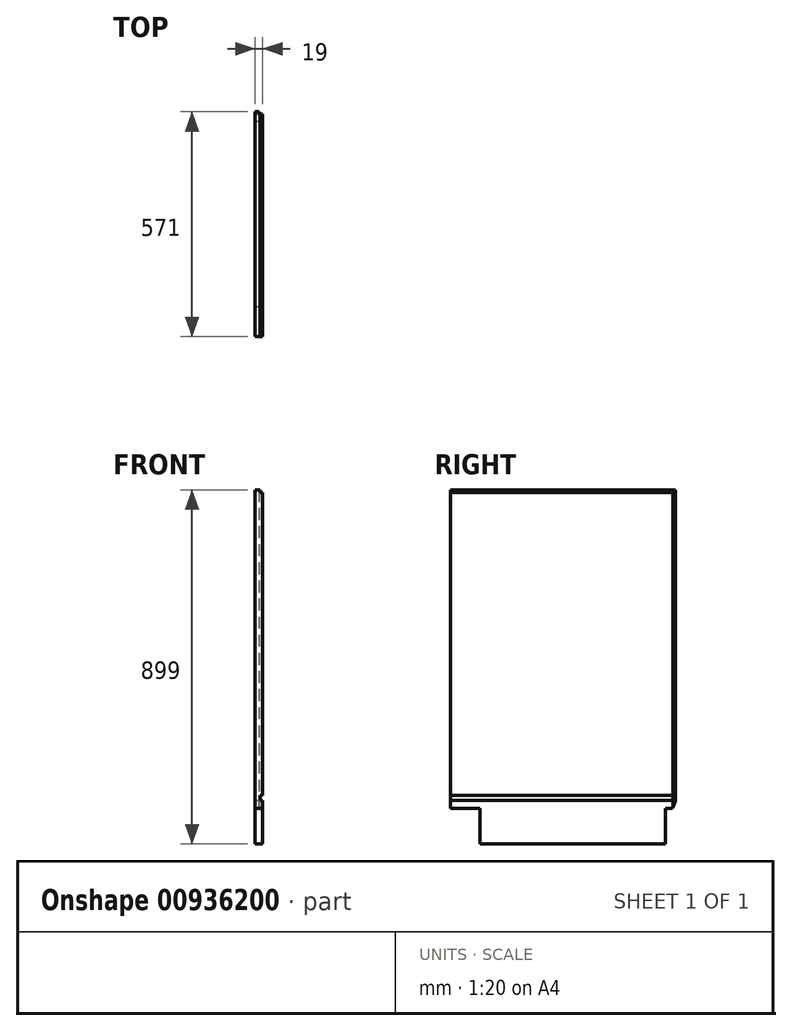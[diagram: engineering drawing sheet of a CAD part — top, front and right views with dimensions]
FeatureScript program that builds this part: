
annotation { "Feature Type Name" : "Feature", "Feature Type Description" : "" }
export const myFeature = defineFeature(function(context is Context, id is Id, definition is map)
    precondition{}
    {
        {
            var Q0;
            Q0=qCreatedBy(makeId("Right.planeOp"),FACE);
            var sketch = newSketch(context, id + "F0", { "sketchPlane" : qUnion([Q0])});
            skLineSegment(sketch, "E0.bottom", {"start": v(0, 0) * mm, "end": v(-496, 0) * mm});
            skLineSegment(sketch, "E0.top", {"start": v(0, 899) * mm, "end": v(-571, 899) * mm});
            skLineSegment(sketch, "E0.left", {"start": v(0, 0) * mm, "end": v(0, 899) * mm});
            skLineSegment(sketch, "E0.right", {"start": v(-571, 90) * mm, "end": v(-571, 899) * mm});
            skLineSegment(sketch, "E1", {"start": v(-571, 90) * mm, "end": v(-496, 90) * mm});
            skLineSegment(sketch, "E2", {"start": v(-496, 90) * mm, "end": v(-496, 0) * mm});
            skSolve(sketch);
        }
        {
            var Q0;
            Q0=makeQuery(id+"F0.imprint","IMPRINT",FACE,{"disambiguationData":[TD([[makeQuery(id+"F0.imprint","IMPRINT",EDGE,{"derivedFrom":sQuery(id+"F0.wireOp",EDGE,"E0.bottom")}),-1.0]])]});
            extrude(context, id + "F1", {"entities" : qUnion([Q0]), "depth" : 19 * mm, "offsetDistance" : 25 * mm});
        }
        {
            var Q0;
            Q0=qCreatedBy(makeId("Front.planeOp"),FACE);
            var sketch = newSketch(context, id + "F2", { "sketchPlane" : qUnion([Q0])});
            skLineSegment(sketch, "E3.bottom", {"start": v(13, 122.5) * mm, "end": v(19, 122.5) * mm});
            skLineSegment(sketch, "E3.top", {"start": v(13, 110) * mm, "end": v(19, 110) * mm});
            skLineSegment(sketch, "E3.left", {"start": v(13, 122.5) * mm, "end": v(13, 110) * mm});
            skLineSegment(sketch, "E3.right", {"start": v(19, 122.5) * mm, "end": v(19, 110) * mm});
            skSolve(sketch);
        }
        {
            var Q0;
            Q0 = qSketchRegion(id + "F2", true);
            extrude(context, id + "F3", {"entities" : qUnion([Q0]), "operationType" : NewBodyOperationType.REMOVE, "endBound" : BoundingType.THROUGH_ALL, "depth" : 25 * mm, "offsetDistance" : 25 * mm});
        }
        {
            var Q0;
            Q0=qCreatedBy(makeId("Top.planeOp"),FACE);
            var sketch = newSketch(context, id + "F4", { "sketchPlane" : qUnion([Q0])});
            skLineSegment(sketch, "E4.bottom", {"start": v(9.5, 0) * mm, "end": v(19, 0) * mm});
            skLineSegment(sketch, "E4.top", {"start": v(9.5, -6) * mm, "end": v(19, -6) * mm});
            skLineSegment(sketch, "E4.left", {"start": v(9.5, 0) * mm, "end": v(9.5, -6) * mm});
            skLineSegment(sketch, "E4.right", {"start": v(19, 0) * mm, "end": v(19, -6) * mm});
            skSolve(sketch);
        }
        {
            var Q0;
            Q0 = qSketchRegion(id + "F4", true);
            extrude(context, id + "F5", {"entities" : qUnion([Q0]), "operationType" : NewBodyOperationType.REMOVE, "endBound" : BoundingType.THROUGH_ALL, "depth" : 25 * mm, "offsetDistance" : 25 * mm});
        }
        {
            var Q0;
            Q0=qCreatedBy(makeId("Right.planeOp"),FACE);
            var sketch = newSketch(context, id + "F6", { "sketchPlane" : qUnion([Q0])});
            skLineSegment(sketch, "E5.bottom", {"start": v(0, 0) * mm, "end": v(-25, 0) * mm});
            skLineSegment(sketch, "E5.top", {"start": v(0, 90) * mm, "end": v(-25, 90) * mm, "construction": true});
            skLineSegment(sketch, "E5.left", {"start": v(0, 0) * mm, "end": v(0, 109) * mm});
            skLineSegment(sketch, "E5.right", {"start": v(-25, 0) * mm, "end": v(-25, 90) * mm});
            skLineSegment(sketch, "E6", {"start": v(0, 109) * mm, "end": v(-6.92, 90) * mm});
            skLineSegment(sketch, "E7", {"start": v(-6.92, 90) * mm, "end": v(-25, 90) * mm});
            skSolve(sketch);
        }
        {
            var Q0;
            Q0 = qSketchRegion(id + "F6", true);
            extrude(context, id + "F7", {"entities" : qUnion([Q0]), "operationType" : NewBodyOperationType.REMOVE, "endBound" : BoundingType.THROUGH_ALL, "depth" : 25 * mm, "offsetDistance" : 25 * mm});
        }
        {
            var Q0;
            Q0=qCreatedBy(makeId("Front.planeOp"),FACE);
            var sketch = newSketch(context, id + "F8", { "sketchPlane" : qUnion([Q0])});
            skLineSegment(sketch, "E8.0", {"start": v(19, 899) * mm, "end": v(0, 899) * mm, "construction": true});
            skLineSegment(sketch, "E8.1", {"start": v(19, 122.5) * mm, "end": v(19, 899) * mm, "construction": true});
            skLineSegment(sketch, "E9.bottom", {"start": v(19, 899) * mm, "end": v(13, 899) * mm});
            skLineSegment(sketch, "E9.top", {"start": v(19, 893) * mm, "end": v(13, 893) * mm});
            skLineSegment(sketch, "E9.left", {"start": v(19, 899) * mm, "end": v(19, 893) * mm});
            skLineSegment(sketch, "E9.right", {"start": v(13, 899) * mm, "end": v(13, 893) * mm});
            skSolve(sketch);
        }
        {
            var Q0;
            Q0 = qSketchRegion(id + "F8", true);
            extrude(context, id + "F9", {"entities" : qUnion([Q0]), "operationType" : NewBodyOperationType.REMOVE, "endBound" : BoundingType.THROUGH_ALL, "depth" : 25 * mm, "offsetDistance" : 25 * mm});
        }
    });
